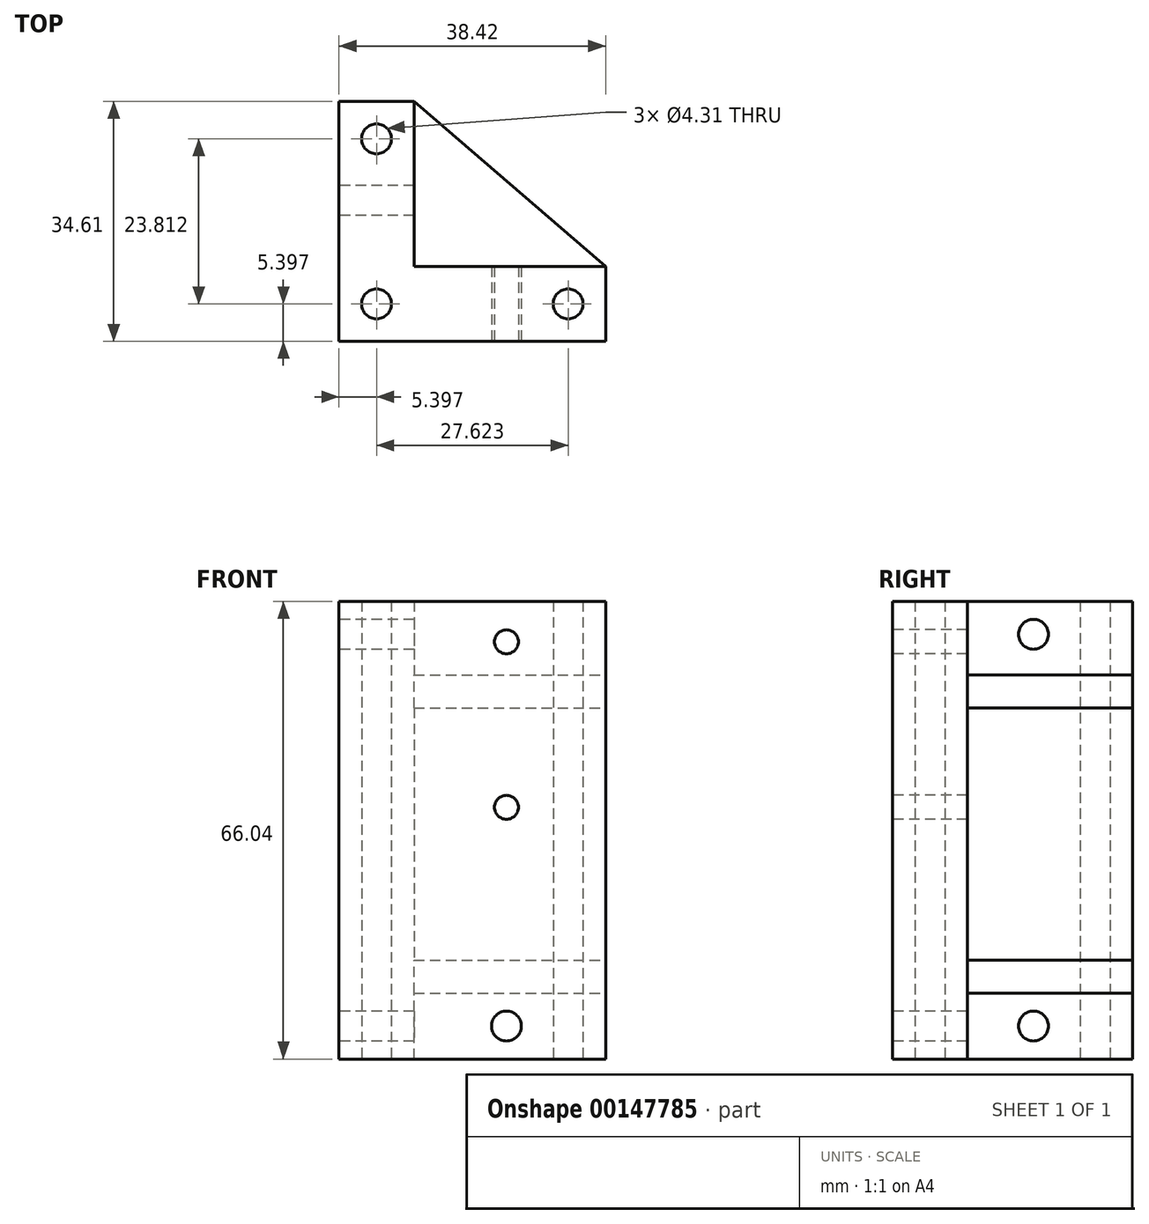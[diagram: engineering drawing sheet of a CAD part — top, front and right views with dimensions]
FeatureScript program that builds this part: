
annotation { "Feature Type Name" : "Feature", "Feature Type Description" : "" }
export const myFeature = defineFeature(function(context is Context, id is Id, definition is map)
    precondition{}
    {
        {
            var Q0;
            Q0=qCreatedBy(makeId("Top.planeOp"),FACE);
            var sketch = newSketch(context, id + "F0", { "sketchPlane" : qUnion([Q0])});
            skLineSegment(sketch, "E0.bottom", {"start": v(0, 0) * mm, "end": v(38.42, 0) * mm});
            skLineSegment(sketch, "E0.left", {"start": v(0, 0) * mm, "end": v(0, 34.6) * mm});
            skLineSegment(sketch, "E1.top", {"start": v(38.42, 10.8) * mm, "end": v(10.8, 10.8) * mm, "construction": true});
            skLineSegment(sketch, "E1.right", {"start": v(10.8, 34.6) * mm, "end": v(10.8, 10.8) * mm, "construction": true});
            skLineSegment(sketch, "E2", {"start": v(0, 34.6) * mm, "end": v(10.8, 34.6) * mm});
            skLineSegment(sketch, "E3", {"start": v(38.42, 10.8) * mm, "end": v(38.42, 0) * mm});
            skLineSegment(sketch, "E4", {"start": v(5.4, 0) * mm, "end": v(5.4, 5.4) * mm, "construction": true});
            skLineSegment(sketch, "E5", {"start": v(5.4, 5.4) * mm, "end": v(0, 5.4) * mm, "construction": true});
            skLineSegment(sketch, "E6", {"start": v(5.4, 5.4) * mm, "end": v(5.4, 29.21) * mm, "construction": true});
            skLineSegment(sketch, "E7", {"start": v(5.4, 29.21) * mm, "end": v(5.4, 34.6) * mm, "construction": true});
            skLineSegment(sketch, "E8", {"start": v(5.4, 5.4) * mm, "end": v(33.02, 5.4) * mm, "construction": true});
            skLineSegment(sketch, "E9", {"start": v(33.02, 5.4) * mm, "end": v(38.42, 5.4) * mm, "construction": true});
            skCircle(sketch, "E10", {"center": v(5.4, 29.21) * mm, "radius": 2.15 * mm});
            skCircle(sketch, "E11", {"center": v(5.4, 5.4) * mm, "radius": 2.15 * mm});
            skCircle(sketch, "E12", {"center": v(33.02, 5.4) * mm, "radius": 2.15 * mm});
            skLineSegment(sketch, "E13", {"start": v(10.8, 34.6) * mm, "end": v(38.42, 34.6) * mm});
            skLineSegment(sketch, "E14", {"start": v(38.42, 34.6) * mm, "end": v(38.42, 10.8) * mm});
            skSolve(sketch);
        }
        {
            var Q0;
            Q0=qSketchRegion(id+"F0",true);
            extrude(context, id + "F1", {"entities" : qUnion([Q0]), "depth" : 66.04 * mm});
        }
        {
            var Q0;
            Q0=makeQuery(id+"F1.opExtrude","SWEPT_FACE",FACE,{"disambiguationData":[OSD([sQuery(id+"F0.wireOp",EDGE,"E0.bottom")])]});
            var sketch = newSketch(context, id + "F2", { "sketchPlane" : qUnion([Q0])});
            skLineSegment(sketch, "E15", {"start": v(24.13, 66.04) * mm, "end": v(24.13, 60.2) * mm, "construction": true});
            skLineSegment(sketch, "E16", {"start": v(24.13, 60.2) * mm, "end": v(0, 60.2) * mm, "construction": true});
            skLineSegment(sketch, "E17", {"start": v(24.13, 60.2) * mm, "end": v(24.13, 36.32) * mm, "construction": true});
            skCircle(sketch, "E18", {"center": v(24.13, 60.2) * mm, "radius": 1.73 * mm});
            skCircle(sketch, "E19", {"center": v(24.13, 36.32) * mm, "radius": 1.73 * mm});
            skLineSegment(sketch, "E20", {"start": v(24.13, 0) * mm, "end": v(24.13, 4.76) * mm, "construction": true});
            skLineSegment(sketch, "E21", {"start": v(24.13, 4.76) * mm, "end": v(38.42, 4.76) * mm, "construction": true});
            skCircle(sketch, "E22", {"center": v(24.13, 4.76) * mm, "radius": 2.15 * mm});
            skSolve(sketch);
        }
        {
            var Q0;
            Q0=qSketchRegion(id+"F2",true);
            var Q1;
            Q1=makeQuery(id+"F1.opExtrude","SWEPT_FACE",FACE,{"disambiguationData":[OSD([sQuery(id+"F0.wireOp",EDGE,"E2"),sQuery(id+"F0.wireOp",EDGE,"E13")])]});
            extrude(context, id + "F3", {"entities" : qUnion([Q0]), "operationType" : NewBodyOperationType.REMOVE, "endBound" : BoundingType.UP_TO_SURFACE, "oppositeDirection" : true, "endBoundEntityFace" : qUnion([Q1]), "depth" : 25.4 * mm});
        }
        {
            var Q0;
            Q0=makeQuery(id+"F1.opExtrude","SWEPT_FACE",FACE,{"disambiguationData":[OSD([sQuery(id+"F0.wireOp",EDGE,"E0.left")])]});
            var sketch = newSketch(context, id + "F4", { "sketchPlane" : qUnion([Q0])});
            skLineSegment(sketch, "E23", {"start": v(-20.32, 66.04) * mm, "end": v(-20.32, 61.28) * mm, "construction": true});
            skLineSegment(sketch, "E24", {"start": v(-34.6, 61.28) * mm, "end": v(-20.32, 61.28) * mm, "construction": true});
            skLineSegment(sketch, "E25", {"start": v(-20.32, 0) * mm, "end": v(-20.32, 4.76) * mm, "construction": true});
            skCircle(sketch, "E26", {"center": v(-20.32, 61.28) * mm, "radius": 2.15 * mm});
            skCircle(sketch, "E27", {"center": v(-20.32, 4.76) * mm, "radius": 2.15 * mm});
            skSolve(sketch);
        }
        {
            var Q0;
            Q0=qSketchRegion(id+"F4",true);
            var Q1;
            Q1=makeQuery(id+"F1.opExtrude","SWEPT_FACE",FACE,{"disambiguationData":[OSD([sQuery(id+"F0.wireOp",EDGE,"E3"),sQuery(id+"F0.wireOp",EDGE,"E14")])]});
            extrude(context, id + "F5", {"entities" : qUnion([Q0]), "operationType" : NewBodyOperationType.REMOVE, "endBound" : BoundingType.UP_TO_SURFACE, "oppositeDirection" : true, "endBoundEntityFace" : qUnion([Q1]), "depth" : 25.4 * mm});
        }
        {
            var Q0;
            Q0=makeQuery(id+"F1.opExtrude","CAP_FACE",FACE,{"disambiguationData":[OSD([sQuery(id+"F0.wireOp",EDGE,"E0.bottom"),sQuery(id+"F0.wireOp",EDGE,"E0.left"),sQuery(id+"F0.wireOp",EDGE,"E2"),sQuery(id+"F0.wireOp",EDGE,"E3"),sQuery(id+"F0.wireOp",EDGE,"E10"),sQuery(id+"F0.wireOp",EDGE,"E11"),sQuery(id+"F0.wireOp",EDGE,"E12"),sQuery(id+"F0.wireOp",EDGE,"E13"),sQuery(id+"F0.wireOp",EDGE,"E14")])],"isStart":false});
            var sketch = newSketch(context, id + "F6", { "sketchPlane" : qUnion([Q0])});
            skLineSegment(sketch, "E28.bottom", {"start": v(38.42, 34.6) * mm, "end": v(10.8, 34.6) * mm});
            skLineSegment(sketch, "E28.top", {"start": v(38.42, 10.8) * mm, "end": v(10.8, 10.8) * mm, "construction": true});
            skLineSegment(sketch, "E28.left", {"start": v(38.42, 34.6) * mm, "end": v(38.42, 10.8) * mm});
            skLineSegment(sketch, "E28.right", {"start": v(10.8, 34.6) * mm, "end": v(10.8, 10.8) * mm, "construction": true});
            skLineSegment(sketch, "E29", {"start": v(5.4, 29.21) * mm, "end": v(5.4, 34.6) * mm, "construction": true});
            skLineSegment(sketch, "E30", {"start": v(5.4, 29.21) * mm, "end": v(10.8, 29.21) * mm, "construction": true});
            skLineSegment(sketch, "E31", {"start": v(33.02, 5.4) * mm, "end": v(33.02, 10.8) * mm, "construction": true});
            skLineSegment(sketch, "E32", {"start": v(10.8, 34.6) * mm, "end": v(38.42, 10.8) * mm});
            skSolve(sketch);
        }
        {
            var Q0;
            Q0=qSketchRegion(id+"F6",true);
            var Q1;
            Q1=makeQuery(id+"F1.opExtrude","CAP_FACE",FACE,{"disambiguationData":[OSD([sQuery(id+"F0.wireOp",EDGE,"E0.bottom"),sQuery(id+"F0.wireOp",EDGE,"E0.left"),sQuery(id+"F0.wireOp",EDGE,"E2"),sQuery(id+"F0.wireOp",EDGE,"E3"),sQuery(id+"F0.wireOp",EDGE,"E10"),sQuery(id+"F0.wireOp",EDGE,"E11"),sQuery(id+"F0.wireOp",EDGE,"E12"),sQuery(id+"F0.wireOp",EDGE,"E13"),sQuery(id+"F0.wireOp",EDGE,"E14")])],"isStart":true});
            extrude(context, id + "F7", {"entities" : qUnion([Q0]), "operationType" : NewBodyOperationType.REMOVE, "endBound" : BoundingType.UP_TO_SURFACE, "oppositeDirection" : true, "endBoundEntityFace" : qUnion([Q1]), "depth" : 25.4 * mm});
        }
        {
            var Q0;
            Q0=makeQuery(id+"F1.opExtrude","SWEPT_FACE",FACE,{"disambiguationData":[OSD([sQuery(id+"F0.wireOp",EDGE,"E0.left")])]});
            cPlane(context, id + "F8", {"entities" : qUnion([Q0]), "cplaneType" : CPlaneType.OFFSET, "offset" : 10.8 * mm, "oppositeDirection" : true, "width" : 152.4 * mm, "height" : 152.4 * mm});
        }
        {
            var Q0;
            Q0=makeQuery(id+"F1.opExtrude","SWEPT_FACE",FACE,{"disambiguationData":[OSD([sQuery(id+"F0.wireOp",EDGE,"E3"),sQuery(id+"F0.wireOp",EDGE,"E14")])]});
            var sketch = newSketch(context, id + "F9", { "sketchPlane" : qUnion([Q0])});
            skLineSegment(sketch, "E33.bottom", {"start": v(10.8, 66.04) * mm, "end": v(34.6, 66.04) * mm});
            skLineSegment(sketch, "E33.top", {"start": v(10.8, 55.44) * mm, "end": v(34.6, 55.44) * mm});
            skLineSegment(sketch, "E33.left", {"start": v(10.8, 66.04) * mm, "end": v(10.8, 55.44) * mm});
            skLineSegment(sketch, "E33.right", {"start": v(34.6, 66.04) * mm, "end": v(34.6, 55.44) * mm});
            skLineSegment(sketch, "E34.bottom", {"start": v(10.8, 0) * mm, "end": v(34.6, 0) * mm});
            skLineSegment(sketch, "E34.top", {"start": v(10.8, 9.53) * mm, "end": v(34.6, 9.53) * mm});
            skLineSegment(sketch, "E34.left", {"start": v(10.8, 0) * mm, "end": v(10.8, 9.53) * mm});
            skLineSegment(sketch, "E34.right", {"start": v(34.6, 0) * mm, "end": v(34.6, 9.53) * mm});
            skLineSegment(sketch, "E35.bottom", {"start": v(10.8, 50.67) * mm, "end": v(34.6, 50.67) * mm});
            skLineSegment(sketch, "E35.top", {"start": v(10.8, 14.29) * mm, "end": v(34.6, 14.29) * mm});
            skLineSegment(sketch, "E35.left", {"start": v(10.8, 50.67) * mm, "end": v(10.8, 14.29) * mm});
            skLineSegment(sketch, "E35.right", {"start": v(34.6, 50.67) * mm, "end": v(34.6, 14.29) * mm});
            skLineSegment(sketch, "E36", {"start": v(22.7, 55.44) * mm, "end": v(22.7, 50.67) * mm, "construction": true});
            skLineSegment(sketch, "E37", {"start": v(22.7, 14.29) * mm, "end": v(22.7, 9.53) * mm, "construction": true});
            skSolve(sketch);
        }
        {
            var Q0;
            Q0=makeQuery(id+"F9.imprint","IMPRINT",FACE,{"disambiguationData":[TD([[makeQuery(id+"F9.imprint","IMPRINT",EDGE,{"derivedFrom":sQuery(id+"F9.wireOp",EDGE,"E34.bottom")}),1.0]])]});
            var Q1;
            Q1=makeQuery(id+"F9.imprint","IMPRINT",FACE,{"disambiguationData":[TD([[makeQuery(id+"F9.imprint","IMPRINT",EDGE,{"derivedFrom":sQuery(id+"F9.wireOp",EDGE,"E35.bottom")}),-1.0]])]});
            var Q2;
            Q2=makeQuery(id+"F9.imprint","IMPRINT",FACE,{"disambiguationData":[TD([[makeQuery(id+"F9.imprint","IMPRINT",EDGE,{"derivedFrom":sQuery(id+"F9.wireOp",EDGE,"E33.bottom")}),-1.0]])]});
            var Q3;
            Q3=qCreatedBy(id+"F8.planeOp",FACE);
            extrude(context, id + "F10", {"entities" : qUnion([Q0, Q1, Q2]), "operationType" : NewBodyOperationType.REMOVE, "endBound" : BoundingType.UP_TO_SURFACE, "oppositeDirection" : true, "endBoundEntityFace" : qUnion([Q3]), "depth" : 25.4 * mm});
        }
    });
